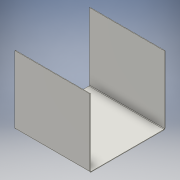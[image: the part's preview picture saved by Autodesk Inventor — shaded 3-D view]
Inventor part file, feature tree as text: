
AUTODESK INVENTOR PART (.ipt)
format: ipt  version: 2018 (Build 220112000, 112)  size: 124,416 bytes
history: native  units: mm
features: sheet_metal_op x7, sketch x3, other x3
ambient origin geometry x8: Origin, YZ Plane, XZ Plane, XY Plane, X Axis, Y Axis, Z Axis, Center Point
bodies: Solid1 (feature_tree)
feature tree (13):
  sheet_metal_op  "Face1"
  sheet_metal_op  "Flange1"
  sheet_metal_op  "Flange2"
  sketch  "Sketch1"  dims[d0=220.0mm]
  other  "Plate1"
  sketch  "Sketch2"  dims[d1=220.0mm]
  other  "Plate2"
  sheet_metal_op  "Bend1"
  sheet_metal_op  "Corner1"
  sketch  "Sketch3"  dims[d2=1.6mm d3=1.6mm d4=0.8mm d5=3.2mm d6=1.6mm d7=200.0mm d8=90.0deg d9=1.6mm d10=6.4mm d11=1.6mm d12=1.6mm d13=1.6mm d14=0.8mm d15=3.2mm d16=1.6mm d17=200.0mm d18=90.0deg d19=1.6mm d20=6.4mm d21=1.6mm d22=1.6mm]
  other  "Plate3"
  sheet_metal_op  "Bend2"
  sheet_metal_op  "Corner2"
